# Revit family: 3L-R-D
name_source: partatom
category: Lighting Fixtures
units: mm (PartAtom-declared; Revit-internal decimal feet)

## family parameters
Cut with Voids When Loaded = No
Host = Face
Light Source = Yes
OmniClass Number = 23.80.70.11.14
OmniClass Title = General Luminaries, Directional
Part Type = Normal
Room Calculation Point = No
Round Connector Dimension = Use Diameter
Shared = No

## types (1)
- 3L-R-D-4-SOF-X-CX-35K-D100
    Apparent Load = 10 VA
    Color Filter = 16777215
    Default Elevation = 4' - 0"
    Description = Mod™ 3 LED Recessed Slot
    Dimming Lamp Color Temperature Shift = <None>
    Downlight diffuse = Soft Diffuse Lens
    Emit Shape Visible in Rendering = No
    Emit from Rectangle Length = 3' - 11"
    Emit from Rectangle Width = 0' - 2 3/4"
    Fixture Option = 3L-R : Carbon Black
    Lamp = LED Lamp
    Length = 4' - 0"
    Load Classification = Lighting
    Manufacturer = Litecontrol
    Model = 3L-R-D
    Photometric Web File = 3L-R-D-4-SOF-X-CX-35K-D100.IES
    Power Factor = 1
    Tilt Angle = -90.00°
    URL = https://www.currentlighting.com
    Voltage = 277 V
    Wattage Comments = Variable Intensity technology provides specifiable lumen output/wattage
    Watts = 10 W
    zzLength1 = 0' - 5 5/8"

## geometry (parser evidence)
native form markers: Blend x8, Sweep x5
no freeform markers — native parametric forms only
